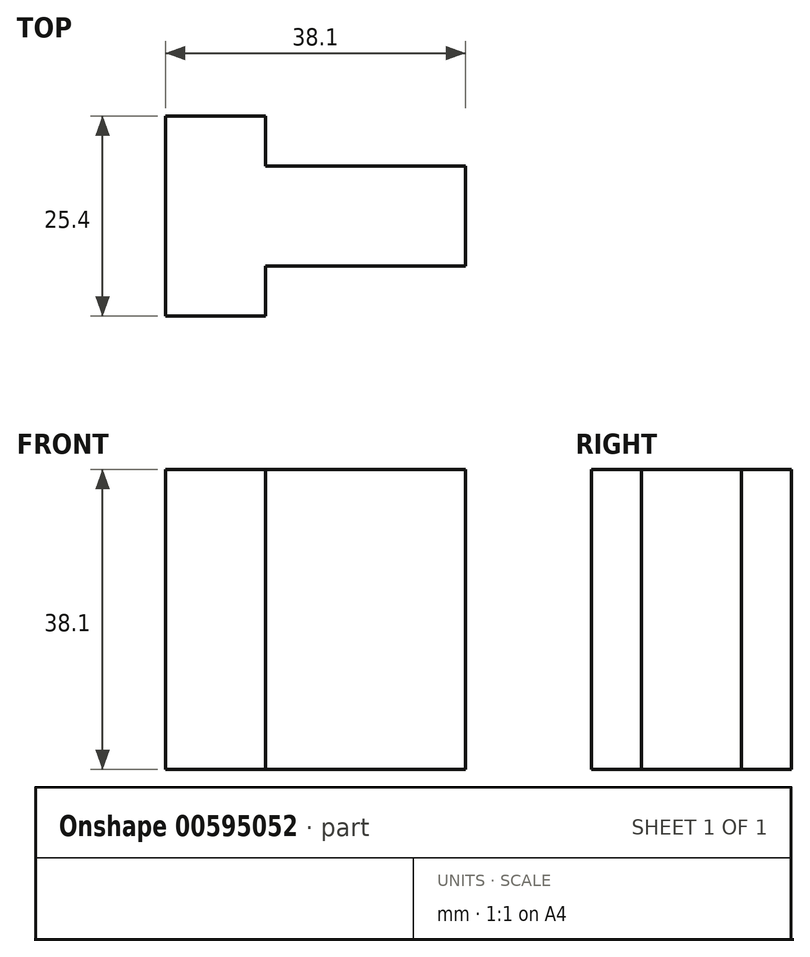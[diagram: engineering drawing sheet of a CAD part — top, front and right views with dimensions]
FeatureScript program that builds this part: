
annotation { "Feature Type Name" : "Feature", "Feature Type Description" : "" }
export const myFeature = defineFeature(function(context is Context, id is Id, definition is map)
    precondition{}
    {
        {
            var Q0;
            Q0=qCreatedBy(makeId("Top.planeOp"),FACE);
            var sketch = newSketch(context, id + "F0", { "sketchPlane" : qUnion([Q0])});
            skLineSegment(sketch, "E0", {"start": v(0, 0) * mm, "end": v(0, 25.4) * mm});
            skLineSegment(sketch, "E1", {"start": v(0, 25.4) * mm, "end": v(12.7, 25.4) * mm});
            skLineSegment(sketch, "E2", {"start": v(12.7, 25.4) * mm, "end": v(12.7, 19.05) * mm});
            skLineSegment(sketch, "E3", {"start": v(12.7, 19.05) * mm, "end": v(38.1, 19.05) * mm});
            skLineSegment(sketch, "E4", {"start": v(38.1, 19.05) * mm, "end": v(38.1, 6.35) * mm});
            skLineSegment(sketch, "E5", {"start": v(38.1, 6.35) * mm, "end": v(12.7, 6.35) * mm});
            skLineSegment(sketch, "E6", {"start": v(12.7, 6.35) * mm, "end": v(12.7, 0) * mm});
            skLineSegment(sketch, "E7", {"start": v(12.7, 0) * mm, "end": v(0, 0) * mm});
            skSolve(sketch);
        }
        {
            var Q0;
            Q0 = qSketchRegion(id + "F0", true);
            extrude(context, id + "F1", {"entities" : qUnion([Q0]), "depth" : 38.1 * mm, "offsetDistance" : 25.4 * mm});
        }
    });
